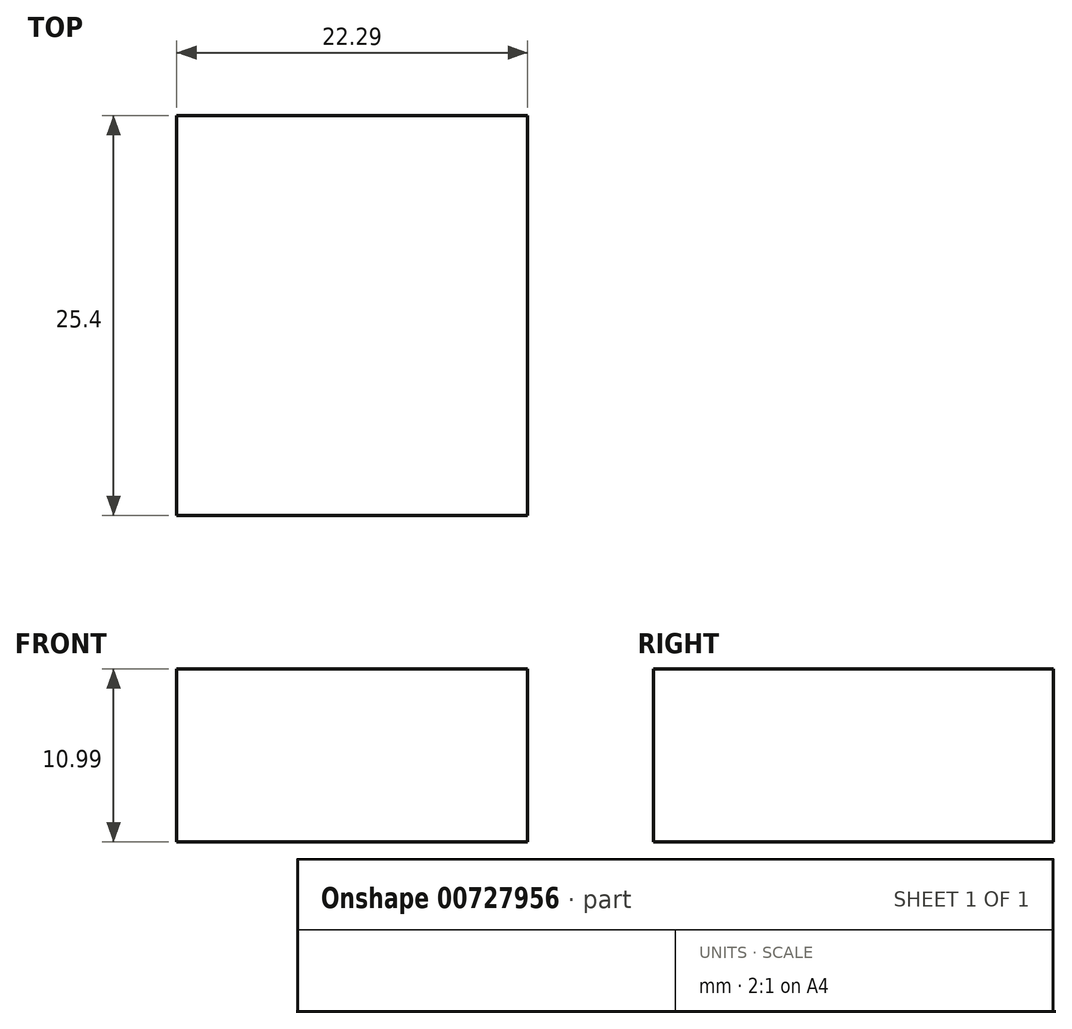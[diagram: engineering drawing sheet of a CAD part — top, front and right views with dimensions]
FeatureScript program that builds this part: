
annotation { "Feature Type Name" : "Feature", "Feature Type Description" : "" }
export const myFeature = defineFeature(function(context is Context, id is Id, definition is map)
    precondition{}
    {
        {
            var Q0;
            Q0=qCreatedBy(makeId("Front.planeOp"),FACE);
            var sketch = newSketch(context, id + "F0", { "sketchPlane" : qUnion([Q0])});
            skLineSegment(sketch, "E0.bottom", {"start": v(-75.89, 0) * mm, "end": v(0, 0) * mm});
            skLineSegment(sketch, "E0.top", {"start": v(-75.89, 76.2) * mm, "end": v(0, 76.2) * mm});
            skLineSegment(sketch, "E0.left", {"start": v(-75.89, 0) * mm, "end": v(-75.89, 76.2) * mm});
            skLineSegment(sketch, "E0.right", {"start": v(0, 0) * mm, "end": v(0, 76.2) * mm});
            skLineSegment(sketch, "E1.bottom", {"start": v(-37.4, -8.4) * mm, "end": v(-59.7, -8.4) * mm});
            skLineSegment(sketch, "E1.top", {"start": v(-37.4, -19.4) * mm, "end": v(-59.7, -19.4) * mm});
            skLineSegment(sketch, "E1.left", {"start": v(-37.4, -8.4) * mm, "end": v(-37.4, -19.4) * mm});
            skLineSegment(sketch, "E1.right", {"start": v(-59.7, -8.4) * mm, "end": v(-59.7, -19.4) * mm});
            skSolve(sketch);
        }
        {
            var Q0;
            Q0=makeQuery(id+"F0.imprint","IMPRINT",FACE,{"disambiguationData":[TD([[makeQuery(id+"F0.imprint","IMPRINT",EDGE,{"derivedFrom":sQuery(id+"F0.wireOp",EDGE,"E1.bottom")}),1.0]])]});
            extrude(context, id + "F1", {"entities" : qUnion([Q0]), "depth" : 25.4 * mm, "offsetDistance" : 25.4 * mm});
        }
    });
